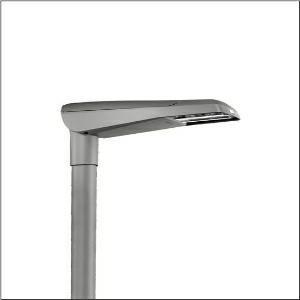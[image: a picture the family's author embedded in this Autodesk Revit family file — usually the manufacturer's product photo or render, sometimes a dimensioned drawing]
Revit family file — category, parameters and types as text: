
# Revit family: streetlight_sl_11_iq_micro___p1_0a_5xc1c51e08ce_6305
name_source: partatom
category: Lighting Fixtures
units: mm (PartAtom-declared; Revit-internal decimal feet)

## family parameters
Cut with Voids When Loaded = No
Host = Face
Light Source = No
Part Type = Normal
Room Calculation Point = No
Round Connector Dimension = Use Diameter
Shared = No

## types (1)
- --- (1 x LED, 1600 lm, 10.8 W, 3000K)
    Apparent Load = 11 VA
    CIE Flux Codes = 29 63 93 100 100
    Color Rendering = 70
    Color Temperature = 3000K
    Default Elevation = 1800 mm
    Description = Streetlight SL 11 iQ micro, mast luminaire, primary light control with 3 zone facetted reflector, of plastic, silver coated, highly specular, primary optical cover: cover, of PMMA, transparent, light distribution: P1.0a, light emission: direct distribution, primary light characteristic: asymmetric, installation type: post-top, side-entry, lamps: LED, High Power LED, rated values: 1.600lm | 10,8W | 148,1lm/W (begin service life); end service life: 1.600lm | 11,1W; at 50% lumin. flux: 800lm | 6W | 133,3lm/W, colour temperature: 3000K, colour rendering: CRI > 70, light colour: 730, light setting 1 begin service life: 100% | 1.600lm | 10,8W | 148,1lm/W | 3.000K, light setting 1 end service life: 11,1W, further light settings possible, control: optimised constant luminous flux control (CLO 2.0), Desk-Remote (wireless, voltage-free reading and setting of iQ features in the workshop via application-optimized NFC function/RFID function), Light-Fading, Smart-Wire, Night-Set, Lumen-Switch, Temp-Guard, Auto-Match, with cable H07RN-F 5x 1.5mm², mains connection: 230..240V, AC, 50/60Hz, connection cable pre-assembled, cable length: 5,5m, luminaire housing, of diecast aluminium, powder-coated, Siteco® metallic grey (DB 702S), please order mast flange separately, inclination adjustable without tools: 0°, 5°, 10°, 15° (post-top) | 0°, -5°, -10°, -15° (side-entry), sealing non-destructively replaceable, multi-level sealing system, length: 600mm, width: 174mm, height: 116mm, mast flange for spigot size: 42mm (side-entry): 5XC10008XM4, 60/48mm (side-entry/post-top): 5XC10108XM2, 76/60mm (side-entry/post-top): 5XC10108XM1, equipment: standard, protection rating (complete): IP66, insulation class (complete): insulation class II (safety insulation), certification: CE, ENEC, ENEC+, VDE, impact resistance: IK10, permissible operating ambient temperature for outdoor applications: -25..+50°C, standard-compliant lighting for roads and squares, Environmental Product Declaration (EPD) tested and certified by an independent institute, packaging unit: 1 piece

Light Distribution: P1.0a
    Height = 116 mm
    Lamp = 1 x LED
    Lamp Light Flux = 1600 lm
    Lamp Power = 10.8 W
    Lamp count = 1
    Length = 600 mm
    Luminous efficacy = 148 lm/W
    Manufacturer = Siteco
    ModVariant = No
    Model = 5XC1C51E08CE
    Number of Poles = 1
    OnlyDefault = Yes
    Power Factor = 1
    Product Name = Streetlight SL 11 iQ micro | P1.0a
    Product group = mast luminaire | pylon top
    ProductGroupID = 6100
    Protection Class = Protection class II
    Protection Degree = IP 66
    RLX_Detail_Level = 1
    RLX_Emergency_Light_Flux = 0 lm
    RLX_Emergency_Type = 0
    RLX_Emergency_Type_DB = No
    RlxData = <blob elided: 26605 chars, md5=57d28049>
    Socket = socket
    Standby Power = 0 W
    System Light Flux = 1600 lm
    System Power = 11 W
    Type Comments = factory setting: luminous flux: 100 % | dim-lin: 254 | 194 mA
    Type Image = l_1006566.jpg
    URL = http://relux.com
    VarID = @adj_001127
    Voltage = 0 V
    Weight = 0.00 kg
    Width = 174 mm

## geometry (parser evidence)
native form markers: Blend x4, Sweep x9
no freeform markers — native parametric forms only
